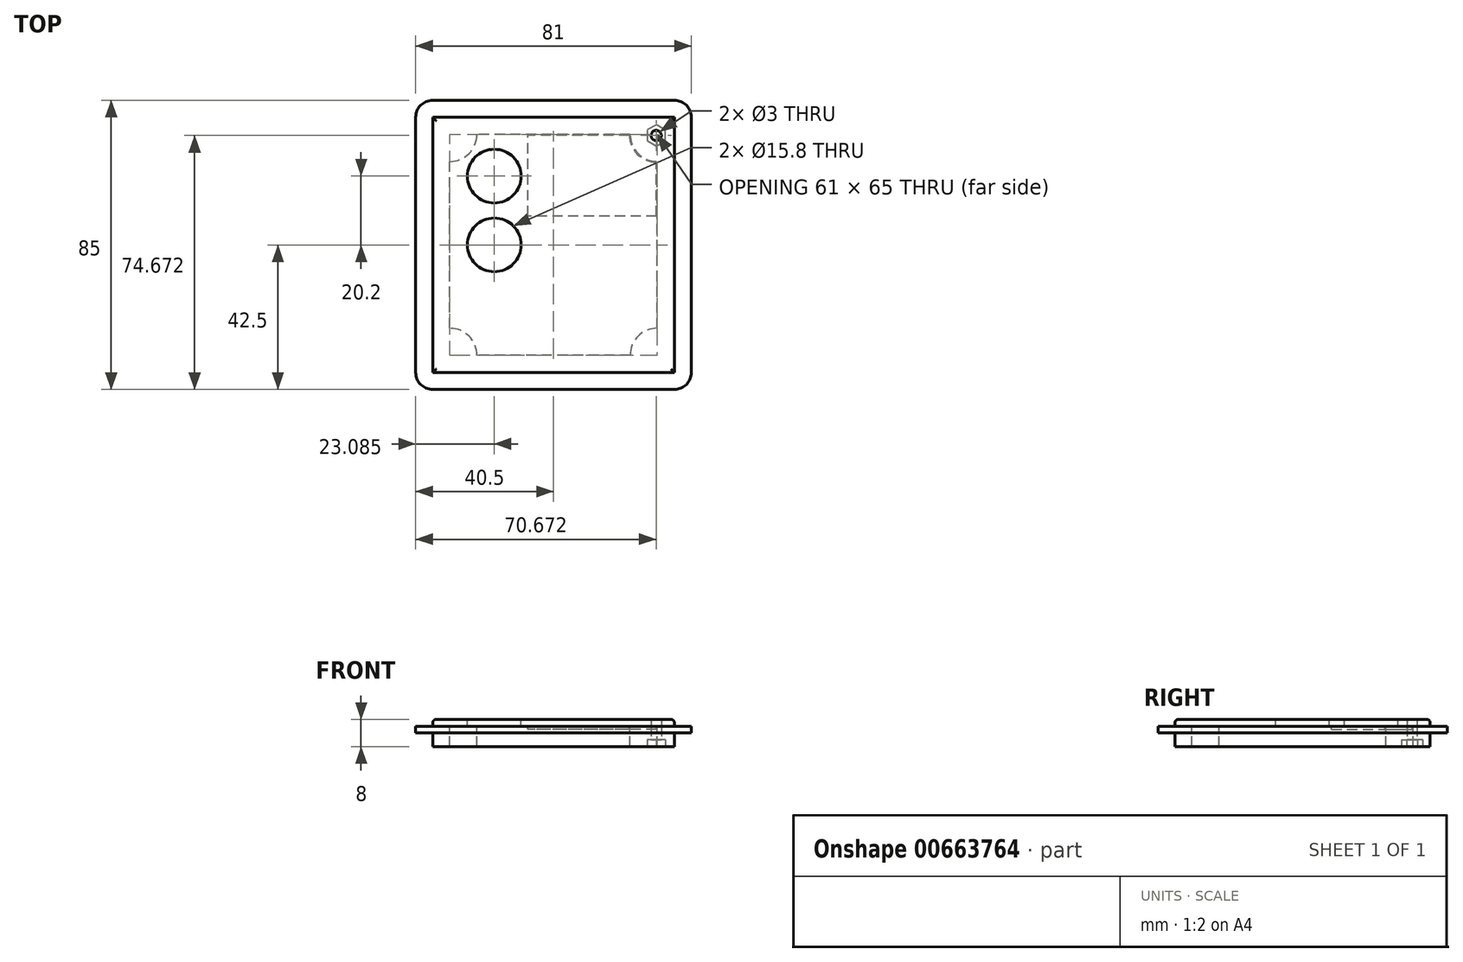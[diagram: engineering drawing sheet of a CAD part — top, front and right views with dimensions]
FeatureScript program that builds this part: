
annotation { "Feature Type Name" : "Feature", "Feature Type Description" : "" }
export const myFeature = defineFeature(function(context is Context, id is Id, definition is map)
    precondition{}
    {
        {
            var Q0;
            Q0=qCreatedBy(makeId("Top.planeOp"),FACE);
            var sketch = newSketch(context, id + "F0", { "sketchPlane" : qUnion([Q0])});
            skLineSegment(sketch, "E0.bottom", {"start": v(35.5, -37.5) * mm, "end": v(-35.5, -37.5) * mm});
            skLineSegment(sketch, "E0.top", {"start": v(35.5, 37.5) * mm, "end": v(-35.5, 37.5) * mm});
            skLineSegment(sketch, "E0.left", {"start": v(35.5, -37.5) * mm, "end": v(35.5, 37.5) * mm});
            skLineSegment(sketch, "E0.right", {"start": v(-35.5, -37.5) * mm, "end": v(-35.5, 37.5) * mm});
            skPoint(sketch, "E0.middle", {"position": v(0, 0) * mm});
            skSolve(sketch);
        }
        {
            var Q0;
            Q0=qSketchRegion(id+"F0",true);
            extrude(context, id + "F1", {"entities" : qUnion([Q0]), "depth" : 4 * mm, "offsetDistance" : 25 * mm});
        }
        {
            var Q0;
            Q0=makeQuery(id+"F1.opExtrude","CAP_FACE",FACE,{"disambiguationData":[OSD([sQuery(id+"F0.wireOp",EDGE,"E0.bottom"),sQuery(id+"F0.wireOp",EDGE,"E0.top"),sQuery(id+"F0.wireOp",EDGE,"E0.left"),sQuery(id+"F0.wireOp",EDGE,"E0.right")])],"isStart":false});
            var sketch = newSketch(context, id + "F2", { "sketchPlane" : qUnion([Q0])});
            skLineSegment(sketch, "E1.bottom", {"start": v(30.5, -32.5) * mm, "end": v(22.5, -32.5) * mm, "construction": true});
            skLineSegment(sketch, "E1.top", {"start": v(30.5, 32.5) * mm, "end": v(22.5, 32.5) * mm, "construction": true});
            skLineSegment(sketch, "E1.left", {"start": v(30.5, -32.5) * mm, "end": v(30.5, -24.5) * mm, "construction": true});
            skLineSegment(sketch, "E1.right", {"start": v(-30.5, -32.5) * mm, "end": v(-30.5, -24.5) * mm, "construction": true});
            skPoint(sketch, "E1.middle", {"position": v(0, 0) * mm});
            skArc(sketch, "E2", {"start": v(-30.5, 24.5) * mm, "mid": v(-24.84, 26.84) * mm, "end": v(-22.5, 32.5) * mm});
            skLineSegment(sketch, "E3", {"start": v(-22.5, 32.5) * mm, "end": v(-30.5, 32.5) * mm, "construction": true});
            skLineSegment(sketch, "E4", {"start": v(-30.5, 24.5) * mm, "end": v(-30.5, 32.5) * mm, "construction": true});
            skArc(sketch, "E5.MirrorCS", {"start": v(30.5, 24.5) * mm, "mid": v(24.84, 26.84) * mm, "end": v(22.5, 32.5) * mm});
            skArc(sketch, "E6.MirrorCS", {"start": v(-30.5, -24.5) * mm, "mid": v(-24.84, -26.84) * mm, "end": v(-22.5, -32.5) * mm});
            skArc(sketch, "E7.MirrorCS", {"start": v(30.5, -24.5) * mm, "mid": v(24.84, -26.84) * mm, "end": v(22.5, -32.5) * mm});
            skLineSegment(sketch, "E8", {"start": v(-30.5, -24.5) * mm, "end": v(-30.5, 24.5) * mm});
            skLineSegment(sketch, "E9", {"start": v(-22.5, -32.5) * mm, "end": v(-30.5, -32.5) * mm, "construction": true});
            skLineSegment(sketch, "E10", {"start": v(22.5, -32.5) * mm, "end": v(-22.5, -32.5) * mm});
            skLineSegment(sketch, "E11", {"start": v(30.5, -24.5) * mm, "end": v(30.5, 24.5) * mm});
            skLineSegment(sketch, "E12", {"start": v(30.5, 24.5) * mm, "end": v(30.5, 32.5) * mm, "construction": true});
            skLineSegment(sketch, "E13", {"start": v(22.5, 32.5) * mm, "end": v(-22.5, 32.5) * mm});
            skSolve(sketch);
        }
        {
            var Q0;
            Q0=makeQuery(id+"F2.imprint","IMPRINT",FACE,{"disambiguationData":[TD([[makeQuery(id+"F2.imprint","IMPRINT",EDGE,{"derivedFrom":sQuery(id+"F2.wireOp",EDGE,"E2")}),-1.0]])]});
            extrude(context, id + "F3", {"entities" : qUnion([Q0]), "operationType" : NewBodyOperationType.REMOVE, "oppositeDirection" : true, "depth" : 25 * mm, "offsetDistance" : 25 * mm});
        }
        {
            var Q0;
            Q0=makeQuery(id+"F1.opExtrude","CAP_FACE",FACE,{"disambiguationData":[OSD([sQuery(id+"F0.wireOp",EDGE,"E0.bottom"),sQuery(id+"F0.wireOp",EDGE,"E0.top"),sQuery(id+"F0.wireOp",EDGE,"E0.left"),sQuery(id+"F0.wireOp",EDGE,"E0.right")])],"isStart":false});
            var sketch = newSketch(context, id + "F4", { "sketchPlane" : qUnion([Q0])});
            skLineSegment(sketch, "E14.bottom", {"start": v(35.5, -42.5) * mm, "end": v(-35.5, -42.5) * mm});
            skLineSegment(sketch, "E14.top", {"start": v(35.5, 42.5) * mm, "end": v(-35.5, 42.5) * mm});
            skLineSegment(sketch, "E14.left", {"start": v(40.5, -37.5) * mm, "end": v(40.5, 37.5) * mm});
            skLineSegment(sketch, "E14.right", {"start": v(-40.5, -37.5) * mm, "end": v(-40.5, 37.5) * mm});
            skPoint(sketch, "E14.middle", {"position": v(0, 0) * mm});
            skPoint(sketch, "E15.visualSharp", {"position": v(-40.5, 42.5) * mm});
            skArc(sketch, "E15.filletArc", {"start": v(-35.5, 42.5) * mm, "mid": v(-39.04, 41.04) * mm, "end": v(-40.5, 37.5) * mm});
            skPoint(sketch, "E16.visualSharp", {"position": v(40.5, 42.5) * mm});
            skArc(sketch, "E16.filletArc", {"start": v(40.5, 37.5) * mm, "mid": v(39.04, 41.04) * mm, "end": v(35.5, 42.5) * mm});
            skPoint(sketch, "E17.visualSharp", {"position": v(40.5, -42.5) * mm});
            skArc(sketch, "E17.filletArc", {"start": v(35.5, -42.5) * mm, "mid": v(39.04, -41.04) * mm, "end": v(40.5, -37.5) * mm});
            skPoint(sketch, "E18.visualSharp", {"position": v(-40.5, -42.5) * mm});
            skArc(sketch, "E18.filletArc", {"start": v(-40.5, -37.5) * mm, "mid": v(-39.04, -41.04) * mm, "end": v(-35.5, -42.5) * mm});
            skArc(sketch, "E19.0", {"start": v(-30.5, 24.5) * mm, "mid": v(-24.84, 26.84) * mm, "end": v(-22.5, 32.5) * mm});
            skLineSegment(sketch, "E19.1", {"start": v(22.5, 32.5) * mm, "end": v(-22.5, 32.5) * mm});
            skArc(sketch, "E19.2", {"start": v(30.5, 24.5) * mm, "mid": v(24.84, 26.84) * mm, "end": v(22.5, 32.5) * mm});
            skLineSegment(sketch, "E19.3", {"start": v(30.5, -24.5) * mm, "end": v(30.5, 24.5) * mm});
            skArc(sketch, "E19.4", {"start": v(30.5, -24.5) * mm, "mid": v(24.84, -26.84) * mm, "end": v(22.5, -32.5) * mm});
            skLineSegment(sketch, "E19.5", {"start": v(22.5, -32.5) * mm, "end": v(-22.5, -32.5) * mm});
            skArc(sketch, "E19.6", {"start": v(-30.5, -24.5) * mm, "mid": v(-24.84, -26.84) * mm, "end": v(-22.5, -32.5) * mm});
            skLineSegment(sketch, "E19.7", {"start": v(-30.5, -24.5) * mm, "end": v(-30.5, 24.5) * mm});
            skSolve(sketch);
        }
        {
            var Q0;
            Q0=qSketchRegion(id+"F4",true);
            extrude(context, id + "F5", {"entities" : qUnion([Q0]), "operationType" : NewBodyOperationType.ADD, "depth" : 2 * mm, "offsetDistance" : 25 * mm});
        }
        {
            var Q0;
            Q0=makeQuery(id+"F1.opExtrude","CAP_FACE",FACE,{"disambiguationData":[OSD([sQuery(id+"F0.wireOp",EDGE,"E0.bottom"),sQuery(id+"F0.wireOp",EDGE,"E0.top"),sQuery(id+"F0.wireOp",EDGE,"E0.left"),sQuery(id+"F0.wireOp",EDGE,"E0.right")])],"isStart":true});
            var sketch = newSketch(context, id + "F6", { "sketchPlane" : qUnion([Q0])});
            skLineSegment(sketch, "E20", {"start": v(35.5, -37.5) * mm, "end": v(24.84, -26.84) * mm, "construction": true});
            skCircle(sketch, "E21.cCircle", {"center": v(30.17, -32.17) * mm, "radius": 2.7 * mm, "construction": true});
            skLineSegment(sketch, "E21.0", {"start": v(27.47, -33.73) * mm, "end": v(27.47, -30.61) * mm});
            skLineSegment(sketch, "E21.1", {"start": v(27.47, -30.61) * mm, "end": v(30.17, -29.05) * mm});
            skLineSegment(sketch, "E21.2", {"start": v(30.17, -29.05) * mm, "end": v(32.87, -30.61) * mm});
            skLineSegment(sketch, "E21.3", {"start": v(32.87, -30.61) * mm, "end": v(32.87, -33.73) * mm});
            skLineSegment(sketch, "E21.4", {"start": v(32.87, -33.73) * mm, "end": v(30.17, -35.29) * mm});
            skLineSegment(sketch, "E21.5", {"start": v(30.17, -35.29) * mm, "end": v(27.47, -33.73) * mm});
            skPoint(sketch, "E21.0.midPoint", {"position": v(27.47, -32.17) * mm});
            skSolve(sketch);
        }
        {
            var Q0;
            Q0=qSketchRegion(id+"F6",true);
            extrude(context, id + "F7", {"entities" : qUnion([Q0]), "operationType" : NewBodyOperationType.REMOVE, "oppositeDirection" : true, "depth" : 2 * mm, "offsetDistance" : 25 * mm});
        }
        {
            var Q0;
            Q0=makeQuery(id+"F5.opExtrude","CAP_FACE",FACE,{"disambiguationData":[OSD([sQuery(id+"F4.wireOp",EDGE,"E14.bottom"),sQuery(id+"F4.wireOp",EDGE,"E14.top"),sQuery(id+"F4.wireOp",EDGE,"E14.left"),sQuery(id+"F4.wireOp",EDGE,"E14.right"),sQuery(id+"F4.wireOp",EDGE,"E15.filletArc"),sQuery(id+"F4.wireOp",EDGE,"E16.filletArc"),sQuery(id+"F4.wireOp",EDGE,"E17.filletArc"),sQuery(id+"F4.wireOp",EDGE,"E18.filletArc"),sQuery(id+"F4.wireOp",EDGE,"E19.0"),sQuery(id+"F4.wireOp",EDGE,"E19.1"),sQuery(id+"F4.wireOp",EDGE,"E19.2"),sQuery(id+"F4.wireOp",EDGE,"E19.3"),sQuery(id+"F4.wireOp",EDGE,"E19.4"),sQuery(id+"F4.wireOp",EDGE,"E19.5"),sQuery(id+"F4.wireOp",EDGE,"E19.6"),sQuery(id+"F4.wireOp",EDGE,"E19.7")])],"isStart":false});
            var sketch = newSketch(context, id + "F8", { "sketchPlane" : qUnion([Q0])});
            skLineSegment(sketch, "E22.bottom", {"start": v(-35.5, 37.5) * mm, "end": v(35.5, 37.5) * mm});
            skLineSegment(sketch, "E22.top", {"start": v(-35.5, -37.5) * mm, "end": v(35.5, -37.5) * mm});
            skLineSegment(sketch, "E22.left", {"start": v(-35.5, 37.5) * mm, "end": v(-35.5, -37.5) * mm});
            skLineSegment(sketch, "E22.right", {"start": v(35.5, 37.5) * mm, "end": v(35.5, -37.5) * mm});
            skPoint(sketch, "E22.middle", {"position": v(0, 0) * mm});
            skLineSegment(sketch, "E23", {"start": v(-30.5, 0) * mm, "end": v(-40.5, 0) * mm});
            skPoint(sketch, "E24", {"position": v(-35.5, 0) * mm});
            skLineSegment(sketch, "E25", {"start": v(0, -42.5) * mm, "end": v(0, -32.5) * mm, "construction": true});
            skPoint(sketch, "E26", {"position": v(0, -37.5) * mm});
            skSolve(sketch);
        }
        {
            var Q0;
            Q0=qSketchRegion(id+"F8",true);
            extrude(context, id + "F9", {"entities" : qUnion([Q0]), "depth" : 2 * mm, "offsetDistance" : 25 * mm});
        }
        {
            var Q0;
            Q0=makeQuery(id+"F1.opExtrude","CAP_FACE",FACE,{"disambiguationData":[OSD([sQuery(id+"F0.wireOp",EDGE,"E0.bottom"),sQuery(id+"F0.wireOp",EDGE,"E0.top"),sQuery(id+"F0.wireOp",EDGE,"E0.left"),sQuery(id+"F0.wireOp",EDGE,"E0.right")])],"isStart":true});
            var sketch = newSketch(context, id + "F10", { "sketchPlane" : qUnion([Q0])});
            skPoint(sketch, "E27.0", {"position": v(30.17, -32.17) * mm});
            skCircle(sketch, "E28", {"center": v(30.17, -32.17) * mm, "radius": 1.5 * mm});
            skSolve(sketch);
        }
        {
            var Q0;
            Q0=qSketchRegion(id+"F10",true);
            extrude(context, id + "F11", {"entities" : qUnion([Q0]), "operationType" : NewBodyOperationType.REMOVE, "oppositeDirection" : true, "depth" : 25 * mm, "offsetDistance" : 25 * mm});
        }
        {
            var Q0;
            Q0=makeQuery(id+"F9.opExtrude","CAP_FACE",FACE,{"disambiguationData":[OSD([sQuery(id+"F8.wireOp",EDGE,"E22.bottom"),sQuery(id+"F8.wireOp",EDGE,"E22.top"),sQuery(id+"F8.wireOp",EDGE,"E22.left"),sQuery(id+"F8.wireOp",EDGE,"E22.right")])],"isStart":false});
            var sketch = newSketch(context, id + "F12", { "sketchPlane" : qUnion([Q0])});
            skCircle(sketch, "E29", {"center": v(-17.41, 20.2) * mm, "radius": 7.9 * mm});
            skCircle(sketch, "E30", {"center": v(-17.41, 0) * mm, "radius": 7.9 * mm});
            skCircle(sketch, "E31", {"center": v(-17.41, -20.2) * mm, "radius": 7.9 * mm, "construction": true});
            skLineSegment(sketch, "E32.0", {"start": v(22.5, 32.5) * mm, "end": v(-22.5, 32.5) * mm, "construction": true});
            skLineSegment(sketch, "E32.1", {"start": v(22.5, -32.5) * mm, "end": v(-22.5, -32.5) * mm, "construction": true});
            skLineSegment(sketch, "E32.2", {"start": v(-30.5, -24.5) * mm, "end": v(-30.5, 24.5) * mm, "construction": true});
            skArc(sketch, "E32.3", {"start": v(-30.5, -24.5) * mm, "mid": v(-24.84, -26.84) * mm, "end": v(-22.5, -32.5) * mm, "construction": true});
            skArc(sketch, "E32.4", {"start": v(-30.5, 24.5) * mm, "mid": v(-24.84, 26.84) * mm, "end": v(-22.5, 32.5) * mm, "construction": true});
            skArc(sketch, "E32.5", {"start": v(30.5, 24.5) * mm, "mid": v(24.84, 26.84) * mm, "end": v(22.5, 32.5) * mm, "construction": true});
            skLineSegment(sketch, "E32.6", {"start": v(30.5, -24.5) * mm, "end": v(30.5, 24.5) * mm, "construction": true});
            skArc(sketch, "E32.7", {"start": v(30.5, -24.5) * mm, "mid": v(24.84, -26.84) * mm, "end": v(22.5, -32.5) * mm, "construction": true});
            skLineSegment(sketch, "E33", {"start": v(-17.41, 32.5) * mm, "end": v(-17.41, 7.9) * mm, "construction": true});
            skPoint(sketch, "E34", {"position": v(-6.45, 20.2) * mm});
            skPoint(sketch, "E35", {"position": v(22.5, 20.2) * mm});
            skSolve(sketch);
        }
        {
            var Q0;
            Q0=qSketchRegion(id+"F12",true);
            extrude(context, id + "F13", {"entities" : qUnion([Q0]), "operationType" : NewBodyOperationType.REMOVE, "oppositeDirection" : true, "depth" : 25 * mm, "offsetDistance" : 25 * mm});
        }
        {
            var Q0;
            {var subQ0=sQuery(id+"F8.wireOp",EDGE,"E22.right");var subQ1=sQuery(id+"F8.wireOp",EDGE,"E22.left");var subQ2=sQuery(id+"F8.wireOp",EDGE,"E22.top");var subQ3=sQuery(id+"F8.wireOp",EDGE,"E22.bottom");var subQ4=makeQuery(id+"F9.opExtrude","CAP_FACE",FACE,{"disambiguationData":[OSD([subQ3,subQ2,subQ1,subQ0])],"isStart":true});Q0=makeQuery(id+"F13.boolean.opBoolean","SPLIT",FACE,{"disambiguationData":[TD([makeQuery(id+"F9.opExtrude","SWEPT_FACE",FACE,{"disambiguationData":[OSD([subQ3])]})])],"derivedFrom":subQ4});}
            var sketch = newSketch(context, id + "F14", { "sketchPlane" : qUnion([Q0])});
            skArc(sketch, "E36.0", {"start": v(30.5, -24.5) * mm, "mid": v(24.84, -26.84) * mm, "end": v(22.5, -32.5) * mm, "construction": true});
            skLineSegment(sketch, "E36.1", {"start": v(22.5, -32.5) * mm, "end": v(-22.5, -32.5) * mm, "construction": true});
            skLineSegment(sketch, "E36.2", {"start": v(30.5, 24.5) * mm, "end": v(30.5, -24.5) * mm, "construction": true});
            skLineSegment(sketch, "E37.0", {"start": v(22.25, -32.25) * mm, "end": v(-7.52, -32.25) * mm});
            skArc(sketch, "E37.1", {"start": v(30.25, -24.25) * mm, "mid": v(24.67, -26.67) * mm, "end": v(22.25, -32.25) * mm});
            skLineSegment(sketch, "E38", {"start": v(30.25, -8.5) * mm, "end": v(30.25, -24.25) * mm});
            skLineSegment(sketch, "E39", {"start": v(30.25, -8.5) * mm, "end": v(-7.52, -8.5) * mm});
            skLineSegment(sketch, "E40", {"start": v(-7.52, -8.5) * mm, "end": v(-7.52, -32.25) * mm});
            skSolve(sketch);
        }
        {
            var Q0;
            Q0=qSketchRegion(id+"F14",true);
            var Q1;
            Q1=qConstructionFilter(qBodyType(qCreatedBy(id+"F14",EDGE),BodyType.WIRE),ConstructionObject.NO);
            extrude(context, id + "F15", {"entities" : qUnion([Q0]), "surfaceEntities" : qUnion([Q1]), "depth" : 0.9 * mm, "offsetDistance" : 25 * mm});
        }
        {
            var Q0;
            Q0=makeQuery(id+"F9.opExtrude","CAP_EDGE",EDGE,{"disambiguationData":[OSD([sQuery(id+"F8.wireOp",EDGE,"E22.top")])],"isStart":false});
            var Q1;
            Q1=makeQuery(id+"F9.opExtrude","CAP_EDGE",EDGE,{"disambiguationData":[OSD([sQuery(id+"F8.wireOp",EDGE,"E22.left")])],"isStart":false});
            var Q2;
            Q2=makeQuery(id+"F9.opExtrude","CAP_EDGE",EDGE,{"disambiguationData":[OSD([sQuery(id+"F8.wireOp",EDGE,"E22.right")])],"isStart":false});
            var Q3;
            Q3=makeQuery(id+"F9.opExtrude","CAP_EDGE",EDGE,{"disambiguationData":[OSD([sQuery(id+"F8.wireOp",EDGE,"E22.bottom")])],"isStart":false});
            fillet(context, id + "F16", {"entities" : qUnion([Q0, Q1, Q2, Q3]), "radius" : 1 * mm, "tangentPropagation" : true, "allowEdgeOverflow" : false});
        }
    });
